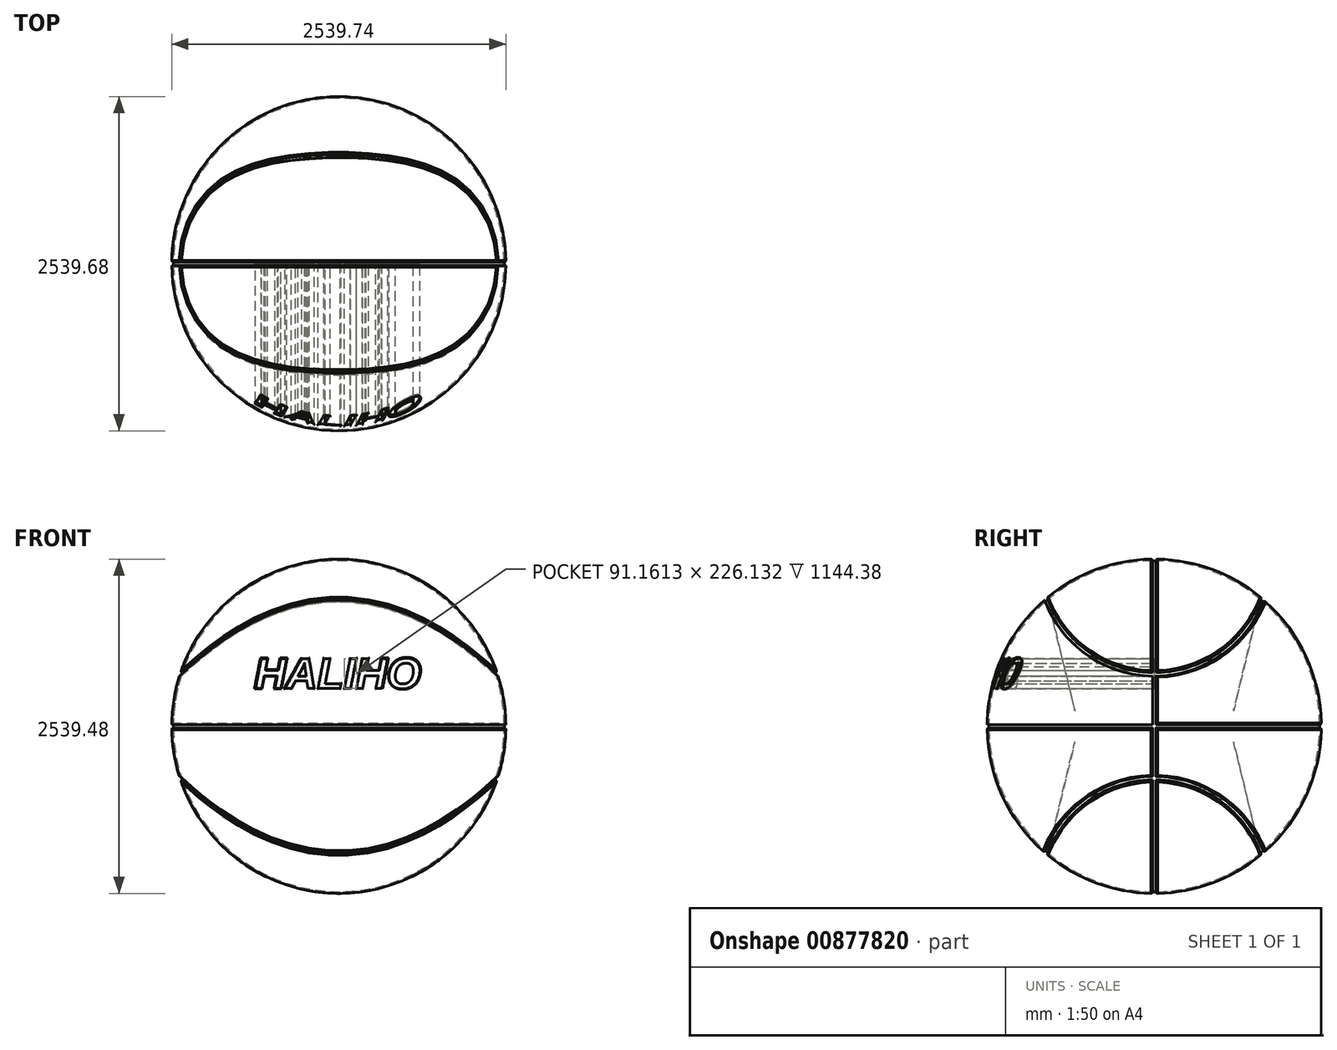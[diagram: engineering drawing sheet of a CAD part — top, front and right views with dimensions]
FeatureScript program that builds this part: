
annotation { "Feature Type Name" : "Feature", "Feature Type Description" : "" }
export const myFeature = defineFeature(function(context is Context, id is Id, definition is map)
    precondition{}
    {
        {
            var Q0;
            Q0=qCreatedBy(makeId("Front.planeOp"),FACE);
            var sketch = newSketch(context, id + "F0", { "sketchPlane" : qUnion([Q0])});
            skArc(sketch, "E0", {"start": v(1270, 0) * mm, "mid": v(0, 1270) * mm, "end": v(-1270, 0) * mm});
            skArc(sketch, "E1", {"start": v(1257.3, 0) * mm, "mid": v(0, 1257.3) * mm, "end": v(-1257.3, 0) * mm});
            skLineSegment(sketch, "E2", {"start": v(1270, 0) * mm, "end": v(-1270, 0) * mm});
            skLineSegment(sketch, "E3", {"start": v(0, 1270) * mm, "end": v(0, 1611.69) * mm});
            skPoint(sketch, "E3.startSnap0", {"position": v(0, 1270) * mm});
            skSolve(sketch);
        }
        {
            var Q0;
            {var subQ0=sQuery(id+"F0.wireOp",EDGE,"E0");Q0=makeQuery(id+"F0.imprint","IMPRINT",FACE,{"disambiguationData":[TD([[makeQuery(id+"F0.imprint","IMPRINT",EDGE,{"derivedFrom":subQ0}),1.0]])]});}
            var Q1;
            Q1=sQuery(id+"F0.wireOp",EDGE,"E2");
            revolve(context, id + "F1", {"surfaceOperationType" : NewSurfaceOperationType.NEW, "entities" : qUnion([Q0]), "axis" : qUnion([Q1]), "revolveType" : RevolveType.FULL});
        }
        {
            var Q0;
            Q0=qCreatedBy(makeId("Right.planeOp"),FACE);
            var sketch = newSketch(context, id + "F2", { "sketchPlane" : qUnion([Q0])});
            skLineSegment(sketch, "E4.bottom", {"start": v(1397, 12.7) * mm, "end": v(-1397, 12.7) * mm});
            skLineSegment(sketch, "E4.top", {"start": v(1397, -12.7) * mm, "end": v(-1397, -12.7) * mm});
            skLineSegment(sketch, "E4.left", {"start": v(1397, 12.7) * mm, "end": v(1397, -12.7) * mm});
            skLineSegment(sketch, "E4.right", {"start": v(-1397, 12.7) * mm, "end": v(-1397, -12.7) * mm});
            skPoint(sketch, "E4.middle", {"position": v(0, 0) * mm});
            skLineSegment(sketch, "E5.bottom", {"start": v(12.7, 1397) * mm, "end": v(-12.7, 1397) * mm});
            skLineSegment(sketch, "E5.top", {"start": v(12.7, -1397) * mm, "end": v(-12.7, -1397) * mm});
            skLineSegment(sketch, "E5.left", {"start": v(12.7, 1397) * mm, "end": v(12.7, -1397) * mm});
            skLineSegment(sketch, "E5.right", {"start": v(-12.7, 1397) * mm, "end": v(-12.7, -1397) * mm});
            skArc(sketch, "E6", {"start": v(-1269.94, 12.7) * mm, "mid": v(-1270, 0) * mm, "end": v(-1269.94, -12.7) * mm});
            skArc(sketch, "E7.trimOffspring", {"start": v(12.7, 1269.94) * mm, "mid": v(0, 1270) * mm, "end": v(-12.7, 1269.94) * mm});
            skArc(sketch, "E8.trimOffspring", {"start": v(1269.94, -12.7) * mm, "mid": v(1270, 0) * mm, "end": v(1269.94, 12.7) * mm});
            skArc(sketch, "E9.trimOffspring", {"start": v(-12.7, -1269.94) * mm, "mid": v(0, -1270) * mm, "end": v(12.7, -1269.94) * mm});
            skCircle(sketch, "E10", {"center": v(0, 1270) * mm, "radius": 889 * mm});
            skCircle(sketch, "E11", {"center": v(0, 1270) * mm, "radius": 863.6 * mm});
            skLineSegment(sketch, "E12", {"start": v(-1397, 0) * mm, "end": v(1397, 0) * mm, "construction": true});
            skCircle(sketch, "E13.MirrorC", {"center": v(0, -1270) * mm, "radius": 889 * mm});
            skCircle(sketch, "E14.MirrorC", {"center": v(0, -1270) * mm, "radius": 863.6 * mm});
            skSolve(sketch);
        }
        {
            var Q0;
            {var subQ0=sQuery(id+"F2.wireOp",EDGE,"E13.MirrorC");var subQ1=sQuery(id+"F2.wireOp",EDGE,"E5.left");var subQ2=makeQuery(id+"F2.imprint","INTERSECT",VERTEX,{"derivedFrom":[subQ1,subQ0]});Q0=makeQuery(id+"F2.imprint","IMPRINT",FACE,{"disambiguationData":[TD([[makeQuery(id+"F2.imprint","IMPRINT",EDGE,{"disambiguationData":[TD([[subQ2,-1.0]])],"derivedFrom":subQ1}),1.0]])]});}
            var Q1;
            {var subQ0=sQuery(id+"F2.wireOp",EDGE,"E10");var subQ1=sQuery(id+"F2.wireOp",EDGE,"E5.left");var subQ2=makeQuery(id+"F2.imprint","INTERSECT",VERTEX,{"derivedFrom":[subQ1,subQ0]});Q1=makeQuery(id+"F2.imprint","IMPRINT",FACE,{"disambiguationData":[TD([[makeQuery(id+"F2.imprint","IMPRINT",EDGE,{"disambiguationData":[TD([[subQ2,1.0]])],"derivedFrom":subQ1}),1.0]])]});}
            var Q2;
            {var subQ0=sQuery(id+"F2.wireOp",EDGE,"E13.MirrorC");var subQ1=sQuery(id+"F2.wireOp",EDGE,"E5.left");var subQ2=makeQuery(id+"F2.imprint","INTERSECT",VERTEX,{"derivedFrom":[subQ1,subQ0]});Q2=makeQuery(id+"F2.imprint","IMPRINT",FACE,{"disambiguationData":[TD([[makeQuery(id+"F2.imprint","IMPRINT",EDGE,{"disambiguationData":[TD([[subQ2,-1.0]])],"derivedFrom":subQ1}),-1.0]])]});}
            var Q3;
            {var subQ0=sQuery(id+"F2.wireOp",EDGE,"E10");var subQ1=sQuery(id+"F2.wireOp",EDGE,"E5.left");var subQ2=makeQuery(id+"F2.imprint","INTERSECT",VERTEX,{"derivedFrom":[subQ1,subQ0]});Q3=makeQuery(id+"F2.imprint","IMPRINT",FACE,{"disambiguationData":[TD([[makeQuery(id+"F2.imprint","IMPRINT",EDGE,{"disambiguationData":[TD([[subQ2,1.0]])],"derivedFrom":subQ1}),-1.0]])]});}
            var Q4;
            {var subQ0=sQuery(id+"F2.wireOp",EDGE,"E9.trimOffspring");Q4=makeQuery(id+"F2.imprint","IMPRINT",FACE,{"disambiguationData":[TD([[makeQuery(id+"F2.imprint","IMPRINT",EDGE,{"derivedFrom":subQ0}),1.0]])]});}
            var Q5;
            {var subQ0=sQuery(id+"F2.wireOp",EDGE,"E8.trimOffspring");Q5=makeQuery(id+"F2.imprint","IMPRINT",FACE,{"disambiguationData":[TD([[makeQuery(id+"F2.imprint","IMPRINT",EDGE,{"derivedFrom":subQ0}),1.0]])]});}
            var Q6;
            {var subQ0=sQuery(id+"F2.wireOp",EDGE,"E5.left");var subQ1=sQuery(id+"F2.wireOp",EDGE,"E4.top");var subQ2=makeQuery(id+"F2.imprint","INTERSECT",VERTEX,{"derivedFrom":[subQ1,subQ0]});Q6=makeQuery(id+"F2.imprint","IMPRINT",FACE,{"disambiguationData":[TD([[makeQuery(id+"F2.imprint","IMPRINT",EDGE,{"disambiguationData":[TD([[subQ2,-1.0]])],"derivedFrom":subQ1}),1.0]])]});}
            var Q7;
            {var subQ0=sQuery(id+"F2.wireOp",EDGE,"E6");Q7=makeQuery(id+"F2.imprint","IMPRINT",FACE,{"disambiguationData":[TD([[makeQuery(id+"F2.imprint","IMPRINT",EDGE,{"derivedFrom":subQ0}),1.0]])]});}
            var Q8;
            {var subQ0=sQuery(id+"F2.wireOp",EDGE,"E7.trimOffspring");Q8=makeQuery(id+"F2.imprint","IMPRINT",FACE,{"disambiguationData":[TD([[makeQuery(id+"F2.imprint","IMPRINT",EDGE,{"derivedFrom":subQ0}),1.0]])]});}
            var Q9;
            {var subQ0=sQuery(id+"F2.wireOp",EDGE,"E5.left");var subQ1=sQuery(id+"F2.wireOp",EDGE,"E4.bottom");var subQ2=makeQuery(id+"F2.imprint","INTERSECT",VERTEX,{"derivedFrom":[subQ1,subQ0]});Q9=makeQuery(id+"F2.imprint","IMPRINT",FACE,{"disambiguationData":[TD([[makeQuery(id+"F2.imprint","IMPRINT",EDGE,{"disambiguationData":[TD([[subQ2,-1.0]])],"derivedFrom":subQ1}),-1.0]])]});}
            var Q10;
            {var subQ0=sQuery(id+"F2.wireOp",EDGE,"E4.right");Q10=makeQuery(id+"F2.imprint","IMPRINT",FACE,{"disambiguationData":[TD([[makeQuery(id+"F2.imprint","IMPRINT",EDGE,{"derivedFrom":subQ0}),1.0]])]});}
            var Q11;
            {var subQ0=sQuery(id+"F2.wireOp",EDGE,"E4.left");Q11=makeQuery(id+"F2.imprint","IMPRINT",FACE,{"disambiguationData":[TD([[makeQuery(id+"F2.imprint","IMPRINT",EDGE,{"derivedFrom":subQ0}),-1.0]])]});}
            var Q12;
            {var subQ0=sQuery(id+"F2.wireOp",EDGE,"E5.bottom");Q12=makeQuery(id+"F2.imprint","IMPRINT",FACE,{"disambiguationData":[TD([[makeQuery(id+"F2.imprint","IMPRINT",EDGE,{"derivedFrom":subQ0}),1.0]])]});}
            var Q13;
            {var subQ0=sQuery(id+"F2.wireOp",EDGE,"E5.top");Q13=makeQuery(id+"F2.imprint","IMPRINT",FACE,{"disambiguationData":[TD([[makeQuery(id+"F2.imprint","IMPRINT",EDGE,{"derivedFrom":subQ0}),-1.0]])]});}
            var Q14;
            {var subQ0=sQuery(id+"F2.wireOp",EDGE,"E5.left");var subQ1=sQuery(id+"F2.wireOp",EDGE,"E4.bottom");var subQ2=makeQuery(id+"F2.imprint","INTERSECT",VERTEX,{"derivedFrom":[subQ1,subQ0]});Q14=makeQuery(id+"F2.imprint","IMPRINT",FACE,{"disambiguationData":[TD([[makeQuery(id+"F2.imprint","IMPRINT",EDGE,{"disambiguationData":[TD([[subQ2,-1.0]])],"derivedFrom":subQ1}),1.0]])]});}
            extrude(context, id + "F3", {"entities" : qUnion([Q0, Q1, Q2, Q3, Q4, Q5, Q6, Q7, Q8, Q9, Q10, Q11, Q12, Q13, Q14]), "operationType" : NewBodyOperationType.REMOVE, "oppositeDirection" : true, "depth" : 5638.8 * mm, "offsetDistance" : 25.4 * mm, "symmetric" : true});
        }
        {
            var Q0;
            {var subQ0=sQuery(id+"F0.wireOp",EDGE,"E1");Q0=makeQuery(id+"F0.imprint","IMPRINT",FACE,{"disambiguationData":[TD([[makeQuery(id+"F0.imprint","IMPRINT",EDGE,{"derivedFrom":subQ0}),1.0]])]});}
            var Q1;
            Q1=sQuery(id+"F0.wireOp",EDGE,"E2");
            revolve(context, id + "F4", {"surfaceOperationType" : NewSurfaceOperationType.NEW, "entities" : qUnion([Q0]), "axis" : qUnion([Q1]), "revolveType" : RevolveType.FULL});
        }
        {
            var Q0;
            Q0=qCreatedBy(makeId("Front.planeOp"),FACE);
            var sketch = newSketch(context, id + "F5", { "sketchPlane" : qUnion([Q0])});
            skText(sketch, "E15", { "text": "HALIHO", "fontName": "Arimo-BoldItalic.ttf"});
            const initialGuessF5  = {"E15": [-0.63861, 0.2874, 1, 0, 0.23666]};
            skSetInitialGuess(sketch, initialGuessF5);
            skSolve(sketch);
        }
        {
            var Q0;
            Q0 = qSketchRegion(id + "F5", true);
            extrude(context, id + "F6", {"entities" : qUnion([Q0]), "operationType" : NewBodyOperationType.REMOVE, "depth" : 3002.28 * mm, "offsetDistance" : 25.4 * mm});
        }
        {
            var Q0;
            {var subQ0=sQuery(id+"F2.wireOp",EDGE,"E5.right");var subQ1=makeQuery(id+"F2.imprint","INTERSECT",VERTEX,{"derivedFrom":[subQ0,sQuery(id+"F2.wireOp",EDGE,"E7.trimOffspring")]});Q0=makeQuery(id+"F3.boolean.opBoolean","SPLIT",FACE,{"disambiguationData":[TD([makeQuery(id+"F3.opExtrude","SWEPT_FACE",FACE,{"disambiguationData":[OSD([subQ0]),TDD([makeQuery(id+"F2.imprint","IMPRINT",EDGE,{"disambiguationData":[TD([[makeQuery(id+"F2.imprint","INTERSECT",VERTEX,{"derivedFrom":[sQuery(id+"F2.wireOp",EDGE,"E5.bottom"),subQ0]}),-1.0]])],"derivedFrom":subQ0}),makeQuery(id+"F2.imprint","IMPRINT",EDGE,{"disambiguationData":[TD([[subQ1,-1.0]])],"derivedFrom":subQ0})])]})])],"derivedFrom":makeQuery(id+"F1.opRevolve","SWEPT_FACE",FACE,{"disambiguationData":[OSD([sQuery(id+"F0.wireOp",EDGE,"E0")])]})});}
            var Q1;
            {var subQ0=sQuery(id+"F2.wireOp",EDGE,"E5.left");var subQ1=makeQuery(id+"F2.imprint","INTERSECT",VERTEX,{"derivedFrom":[subQ0,sQuery(id+"F2.wireOp",EDGE,"E7.trimOffspring")]});Q1=makeQuery(id+"F3.boolean.opBoolean","SPLIT",FACE,{"disambiguationData":[TD([makeQuery(id+"F3.opExtrude","SWEPT_FACE",FACE,{"disambiguationData":[OSD([subQ0]),TDD([makeQuery(id+"F2.imprint","IMPRINT",EDGE,{"disambiguationData":[TD([[makeQuery(id+"F2.imprint","INTERSECT",VERTEX,{"derivedFrom":[sQuery(id+"F2.wireOp",EDGE,"E5.bottom"),subQ0]}),-1.0]])],"derivedFrom":subQ0}),makeQuery(id+"F2.imprint","IMPRINT",EDGE,{"disambiguationData":[TD([[subQ1,-1.0]])],"derivedFrom":subQ0})])]})])],"derivedFrom":makeQuery(id+"F1.opRevolve","SWEPT_FACE",FACE,{"disambiguationData":[OSD([sQuery(id+"F0.wireOp",EDGE,"E0")])]})});}
            var Q2;
            {var subQ0=sQuery(id+"F2.wireOp",EDGE,"E4.bottom");var subQ2=sQuery(id+"F2.wireOp",EDGE,"E5.left");var subQ3=makeQuery(id+"F2.imprint","INTERSECT",VERTEX,{"derivedFrom":[subQ0,subQ2]});Q2=makeQuery(id+"F3.boolean.opBoolean","SPLIT",FACE,{"disambiguationData":[TD([makeQuery(id+"F3.opExtrude","SWEPT_FACE",FACE,{"disambiguationData":[OSD([subQ2]),TDD([makeQuery(id+"F2.imprint","IMPRINT",EDGE,{"disambiguationData":[TD([[subQ3,1.0]])],"derivedFrom":subQ2})])]})])],"derivedFrom":makeQuery(id+"F1.opRevolve","SWEPT_FACE",FACE,{"disambiguationData":[OSD([sQuery(id+"F0.wireOp",EDGE,"E0")])]})});}
            var Q3;
            {var subQ0=sQuery(id+"F2.wireOp",EDGE,"E4.top");var subQ2=sQuery(id+"F2.wireOp",EDGE,"E5.left");var subQ3=makeQuery(id+"F2.imprint","INTERSECT",VERTEX,{"derivedFrom":[subQ0,subQ2]});Q3=makeQuery(id+"F3.boolean.opBoolean","SPLIT",FACE,{"disambiguationData":[TD([makeQuery(id+"F3.opExtrude","SWEPT_FACE",FACE,{"disambiguationData":[OSD([subQ2]),TDD([makeQuery(id+"F2.imprint","IMPRINT",EDGE,{"disambiguationData":[TD([[subQ3,-1.0]])],"derivedFrom":subQ2})])]})])],"derivedFrom":makeQuery(id+"F1.opRevolve","SWEPT_FACE",FACE,{"disambiguationData":[OSD([sQuery(id+"F0.wireOp",EDGE,"E0")])]})});}
            var Q4;
            {var subQ0=sQuery(id+"F2.wireOp",EDGE,"E5.left");var subQ1=makeQuery(id+"F2.imprint","INTERSECT",VERTEX,{"derivedFrom":[subQ0,sQuery(id+"F2.wireOp",EDGE,"E9.trimOffspring")]});Q4=makeQuery(id+"F3.boolean.opBoolean","SPLIT",FACE,{"disambiguationData":[TD([makeQuery(id+"F3.opExtrude","SWEPT_FACE",FACE,{"disambiguationData":[OSD([subQ0]),TDD([makeQuery(id+"F2.imprint","IMPRINT",EDGE,{"disambiguationData":[TD([[subQ1,1.0]])],"derivedFrom":subQ0}),makeQuery(id+"F2.imprint","IMPRINT",EDGE,{"disambiguationData":[TD([[makeQuery(id+"F2.imprint","INTERSECT",VERTEX,{"derivedFrom":[sQuery(id+"F2.wireOp",EDGE,"E5.top"),subQ0]}),1.0]])],"derivedFrom":subQ0})])]})])],"derivedFrom":makeQuery(id+"F1.opRevolve","SWEPT_FACE",FACE,{"disambiguationData":[OSD([sQuery(id+"F0.wireOp",EDGE,"E0")])]})});}
            var Q5;
            {var subQ0=sQuery(id+"F2.wireOp",EDGE,"E5.right");var subQ1=makeQuery(id+"F2.imprint","INTERSECT",VERTEX,{"derivedFrom":[subQ0,sQuery(id+"F2.wireOp",EDGE,"E9.trimOffspring")]});Q5=makeQuery(id+"F3.boolean.opBoolean","SPLIT",FACE,{"disambiguationData":[TD([makeQuery(id+"F3.opExtrude","SWEPT_FACE",FACE,{"disambiguationData":[OSD([subQ0]),TDD([makeQuery(id+"F2.imprint","IMPRINT",EDGE,{"disambiguationData":[TD([[subQ1,1.0]])],"derivedFrom":subQ0}),makeQuery(id+"F2.imprint","IMPRINT",EDGE,{"disambiguationData":[TD([[makeQuery(id+"F2.imprint","INTERSECT",VERTEX,{"derivedFrom":[sQuery(id+"F2.wireOp",EDGE,"E5.top"),subQ0]}),1.0]])],"derivedFrom":subQ0})])]})])],"derivedFrom":makeQuery(id+"F1.opRevolve","SWEPT_FACE",FACE,{"disambiguationData":[OSD([sQuery(id+"F0.wireOp",EDGE,"E0")])]})});}
            var Q6;
            {var subQ0=sQuery(id+"F2.wireOp",EDGE,"E4.top");var subQ2=sQuery(id+"F2.wireOp",EDGE,"E5.right");var subQ3=makeQuery(id+"F2.imprint","INTERSECT",VERTEX,{"derivedFrom":[subQ0,subQ2]});Q6=makeQuery(id+"F3.boolean.opBoolean","SPLIT",FACE,{"disambiguationData":[TD([makeQuery(id+"F3.opExtrude","SWEPT_FACE",FACE,{"disambiguationData":[OSD([subQ2]),TDD([makeQuery(id+"F2.imprint","IMPRINT",EDGE,{"disambiguationData":[TD([[subQ3,-1.0]])],"derivedFrom":subQ2})])]})])],"derivedFrom":makeQuery(id+"F1.opRevolve","SWEPT_FACE",FACE,{"disambiguationData":[OSD([sQuery(id+"F0.wireOp",EDGE,"E0")])]})});}
            var Q7;
            {var subQ0=sQuery(id+"F2.wireOp",EDGE,"E4.bottom");var subQ2=sQuery(id+"F2.wireOp",EDGE,"E5.right");var subQ3=makeQuery(id+"F2.imprint","INTERSECT",VERTEX,{"derivedFrom":[subQ0,subQ2]});Q7=makeQuery(id+"F6.boolean.opBoolean","INTERSECT",EDGE,{"derivedFrom":[makeQuery(id+"F3.boolean.opBoolean","SPLIT",FACE,{"disambiguationData":[TD([makeQuery(id+"F3.opExtrude","SWEPT_FACE",FACE,{"disambiguationData":[OSD([subQ2]),TDD([makeQuery(id+"F2.imprint","IMPRINT",EDGE,{"disambiguationData":[TD([[subQ3,1.0]])],"derivedFrom":subQ2})])]})])],"derivedFrom":makeQuery(id+"F1.opRevolve","SWEPT_FACE",FACE,{"disambiguationData":[OSD([sQuery(id+"F0.wireOp",EDGE,"E1")])]})}),makeQuery(id+"F6.opExtrude","SWEPT_FACE",FACE,{"disambiguationData":[OSD([sQuery(id+"F5.wireOp",EDGE,"E15.sketch_text.stroke-48")])]})]});}
            var Q8;
            {var subQ0=sQuery(id+"F2.wireOp",EDGE,"E4.bottom");var subQ1=makeQuery(id+"F2.imprint","INTERSECT",VERTEX,{"derivedFrom":[subQ0,sQuery(id+"F2.wireOp",EDGE,"E6")]});Q8=makeQuery(id+"F3.boolean.opBoolean","INTERSECT",EDGE,{"derivedFrom":[makeQuery(id+"F1.opRevolve","SWEPT_FACE",FACE,{"disambiguationData":[OSD([sQuery(id+"F0.wireOp",EDGE,"E0")])]}),makeQuery(id+"F3.opExtrude","SWEPT_FACE",FACE,{"disambiguationData":[OSD([subQ0]),TDD([makeQuery(id+"F2.imprint","IMPRINT",EDGE,{"disambiguationData":[TD([[subQ1,1.0]])],"derivedFrom":subQ0}),makeQuery(id+"F2.imprint","IMPRINT",EDGE,{"disambiguationData":[TD([[makeQuery(id+"F2.imprint","INTERSECT",VERTEX,{"derivedFrom":[subQ0,sQuery(id+"F2.wireOp",EDGE,"E4.right")]}),1.0]])],"derivedFrom":subQ0})])]})]});}
            fillet(context, id + "F7", {"entities" : qUnion([Q0, Q1, Q2, Q3, Q4, Q5, Q6, Q7, Q8]), "radius" : 12.7 * mm, "allowEdgeOverflow" : false});
        }
        {
            var Q0;
            {var subQ0=sQuery(id+"F2.wireOp",EDGE,"E4.bottom");var subQ2=sQuery(id+"F2.wireOp",EDGE,"E5.right");var subQ3=makeQuery(id+"F2.imprint","INTERSECT",VERTEX,{"derivedFrom":[subQ0,subQ2]});Q0=makeQuery(id+"F6.boolean.opBoolean","INTERSECT",EDGE,{"derivedFrom":[makeQuery(id+"F3.boolean.opBoolean","SPLIT",FACE,{"disambiguationData":[TD([makeQuery(id+"F3.opExtrude","SWEPT_FACE",FACE,{"disambiguationData":[OSD([subQ2]),TDD([makeQuery(id+"F2.imprint","IMPRINT",EDGE,{"disambiguationData":[TD([[subQ3,1.0]])],"derivedFrom":subQ2})])]})])],"derivedFrom":makeQuery(id+"F1.opRevolve","SWEPT_FACE",FACE,{"disambiguationData":[OSD([sQuery(id+"F0.wireOp",EDGE,"E0")])]})}),makeQuery(id+"F6.opExtrude","SWEPT_FACE",FACE,{"disambiguationData":[OSD([sQuery(id+"F5.wireOp",EDGE,"E15.sketch_text.stroke-56")])]})]});}
            var Q1;
            {var subQ0=sQuery(id+"F2.wireOp",EDGE,"E4.bottom");var subQ2=sQuery(id+"F2.wireOp",EDGE,"E5.right");var subQ3=makeQuery(id+"F2.imprint","INTERSECT",VERTEX,{"derivedFrom":[subQ0,subQ2]});Q1=makeQuery(id+"F6.boolean.opBoolean","INTERSECT",EDGE,{"derivedFrom":[makeQuery(id+"F3.boolean.opBoolean","SPLIT",FACE,{"disambiguationData":[TD([makeQuery(id+"F3.opExtrude","SWEPT_FACE",FACE,{"disambiguationData":[OSD([subQ2]),TDD([makeQuery(id+"F2.imprint","IMPRINT",EDGE,{"disambiguationData":[TD([[subQ3,1.0]])],"derivedFrom":subQ2})])]})])],"derivedFrom":makeQuery(id+"F1.opRevolve","SWEPT_FACE",FACE,{"disambiguationData":[OSD([sQuery(id+"F0.wireOp",EDGE,"E0")])]})}),makeQuery(id+"F6.opExtrude","SWEPT_FACE",FACE,{"disambiguationData":[OSD([sQuery(id+"F5.wireOp",EDGE,"E15.sketch_text.stroke-55")])]})]});}
            var Q2;
            {var subQ0=sQuery(id+"F2.wireOp",EDGE,"E4.bottom");var subQ2=sQuery(id+"F2.wireOp",EDGE,"E5.right");var subQ3=makeQuery(id+"F2.imprint","INTERSECT",VERTEX,{"derivedFrom":[subQ0,subQ2]});Q2=makeQuery(id+"F6.boolean.opBoolean","INTERSECT",EDGE,{"derivedFrom":[makeQuery(id+"F3.boolean.opBoolean","SPLIT",FACE,{"disambiguationData":[TD([makeQuery(id+"F3.opExtrude","SWEPT_FACE",FACE,{"disambiguationData":[OSD([subQ2]),TDD([makeQuery(id+"F2.imprint","IMPRINT",EDGE,{"disambiguationData":[TD([[subQ3,1.0]])],"derivedFrom":subQ2})])]})])],"derivedFrom":makeQuery(id+"F1.opRevolve","SWEPT_FACE",FACE,{"disambiguationData":[OSD([sQuery(id+"F0.wireOp",EDGE,"E0")])]})}),makeQuery(id+"F6.opExtrude","SWEPT_FACE",FACE,{"disambiguationData":[OSD([sQuery(id+"F5.wireOp",EDGE,"E15.sketch_text.stroke-54")])]})]});}
            var Q3;
            {var subQ0=sQuery(id+"F2.wireOp",EDGE,"E4.bottom");var subQ2=sQuery(id+"F2.wireOp",EDGE,"E5.right");var subQ3=makeQuery(id+"F2.imprint","INTERSECT",VERTEX,{"derivedFrom":[subQ0,subQ2]});Q3=makeQuery(id+"F6.boolean.opBoolean","INTERSECT",EDGE,{"derivedFrom":[makeQuery(id+"F3.boolean.opBoolean","SPLIT",FACE,{"disambiguationData":[TD([makeQuery(id+"F3.opExtrude","SWEPT_FACE",FACE,{"disambiguationData":[OSD([subQ2]),TDD([makeQuery(id+"F2.imprint","IMPRINT",EDGE,{"disambiguationData":[TD([[subQ3,1.0]])],"derivedFrom":subQ2})])]})])],"derivedFrom":makeQuery(id+"F1.opRevolve","SWEPT_FACE",FACE,{"disambiguationData":[OSD([sQuery(id+"F0.wireOp",EDGE,"E0")])]})}),makeQuery(id+"F6.opExtrude","SWEPT_FACE",FACE,{"disambiguationData":[OSD([sQuery(id+"F5.wireOp",EDGE,"E15.sketch_text.stroke-53")])]})]});}
            var Q4;
            {var subQ0=sQuery(id+"F2.wireOp",EDGE,"E4.bottom");var subQ2=sQuery(id+"F2.wireOp",EDGE,"E5.right");var subQ3=makeQuery(id+"F2.imprint","INTERSECT",VERTEX,{"derivedFrom":[subQ0,subQ2]});Q4=makeQuery(id+"F6.boolean.opBoolean","INTERSECT",EDGE,{"derivedFrom":[makeQuery(id+"F3.boolean.opBoolean","SPLIT",FACE,{"disambiguationData":[TD([makeQuery(id+"F3.opExtrude","SWEPT_FACE",FACE,{"disambiguationData":[OSD([subQ2]),TDD([makeQuery(id+"F2.imprint","IMPRINT",EDGE,{"disambiguationData":[TD([[subQ3,1.0]])],"derivedFrom":subQ2})])]})])],"derivedFrom":makeQuery(id+"F1.opRevolve","SWEPT_FACE",FACE,{"disambiguationData":[OSD([sQuery(id+"F0.wireOp",EDGE,"E0")])]})}),makeQuery(id+"F6.opExtrude","SWEPT_FACE",FACE,{"disambiguationData":[OSD([sQuery(id+"F5.wireOp",EDGE,"E15.sketch_text.stroke-52")])]})]});}
            var Q5;
            {var subQ0=sQuery(id+"F2.wireOp",EDGE,"E4.bottom");var subQ2=sQuery(id+"F2.wireOp",EDGE,"E5.right");var subQ3=makeQuery(id+"F2.imprint","INTERSECT",VERTEX,{"derivedFrom":[subQ0,subQ2]});Q5=makeQuery(id+"F6.boolean.opBoolean","INTERSECT",EDGE,{"derivedFrom":[makeQuery(id+"F3.boolean.opBoolean","SPLIT",FACE,{"disambiguationData":[TD([makeQuery(id+"F3.opExtrude","SWEPT_FACE",FACE,{"disambiguationData":[OSD([subQ2]),TDD([makeQuery(id+"F2.imprint","IMPRINT",EDGE,{"disambiguationData":[TD([[subQ3,1.0]])],"derivedFrom":subQ2})])]})])],"derivedFrom":makeQuery(id+"F1.opRevolve","SWEPT_FACE",FACE,{"disambiguationData":[OSD([sQuery(id+"F0.wireOp",EDGE,"E0")])]})}),makeQuery(id+"F6.opExtrude","SWEPT_FACE",FACE,{"disambiguationData":[OSD([sQuery(id+"F5.wireOp",EDGE,"E15.sketch_text.stroke-45")])]})]});}
            var Q6;
            {var subQ0=sQuery(id+"F2.wireOp",EDGE,"E4.bottom");var subQ2=sQuery(id+"F2.wireOp",EDGE,"E5.right");var subQ3=makeQuery(id+"F2.imprint","INTERSECT",VERTEX,{"derivedFrom":[subQ0,subQ2]});Q6=makeQuery(id+"F6.boolean.opBoolean","INTERSECT",EDGE,{"derivedFrom":[makeQuery(id+"F3.boolean.opBoolean","SPLIT",FACE,{"disambiguationData":[TD([makeQuery(id+"F3.opExtrude","SWEPT_FACE",FACE,{"disambiguationData":[OSD([subQ2]),TDD([makeQuery(id+"F2.imprint","IMPRINT",EDGE,{"disambiguationData":[TD([[subQ3,1.0]])],"derivedFrom":subQ2})])]})])],"derivedFrom":makeQuery(id+"F1.opRevolve","SWEPT_FACE",FACE,{"disambiguationData":[OSD([sQuery(id+"F0.wireOp",EDGE,"E0")])]})}),makeQuery(id+"F6.opExtrude","SWEPT_FACE",FACE,{"disambiguationData":[OSD([sQuery(id+"F5.wireOp",EDGE,"E15.sketch_text.stroke-44")])]})]});}
            var Q7;
            {var subQ0=sQuery(id+"F2.wireOp",EDGE,"E4.bottom");var subQ2=sQuery(id+"F2.wireOp",EDGE,"E5.right");var subQ3=makeQuery(id+"F2.imprint","INTERSECT",VERTEX,{"derivedFrom":[subQ0,subQ2]});Q7=makeQuery(id+"F6.boolean.opBoolean","INTERSECT",EDGE,{"derivedFrom":[makeQuery(id+"F3.boolean.opBoolean","SPLIT",FACE,{"disambiguationData":[TD([makeQuery(id+"F3.opExtrude","SWEPT_FACE",FACE,{"disambiguationData":[OSD([subQ2]),TDD([makeQuery(id+"F2.imprint","IMPRINT",EDGE,{"disambiguationData":[TD([[subQ3,1.0]])],"derivedFrom":subQ2})])]})])],"derivedFrom":makeQuery(id+"F1.opRevolve","SWEPT_FACE",FACE,{"disambiguationData":[OSD([sQuery(id+"F0.wireOp",EDGE,"E0")])]})}),makeQuery(id+"F6.opExtrude","SWEPT_FACE",FACE,{"disambiguationData":[OSD([sQuery(id+"F5.wireOp",EDGE,"E15.sketch_text.stroke-43")])]})]});}
            var Q8;
            {var subQ0=sQuery(id+"F2.wireOp",EDGE,"E4.bottom");var subQ2=sQuery(id+"F2.wireOp",EDGE,"E5.right");var subQ3=makeQuery(id+"F2.imprint","INTERSECT",VERTEX,{"derivedFrom":[subQ0,subQ2]});Q8=makeQuery(id+"F6.boolean.opBoolean","INTERSECT",EDGE,{"derivedFrom":[makeQuery(id+"F3.boolean.opBoolean","SPLIT",FACE,{"disambiguationData":[TD([makeQuery(id+"F3.opExtrude","SWEPT_FACE",FACE,{"disambiguationData":[OSD([subQ2]),TDD([makeQuery(id+"F2.imprint","IMPRINT",EDGE,{"disambiguationData":[TD([[subQ3,1.0]])],"derivedFrom":subQ2})])]})])],"derivedFrom":makeQuery(id+"F1.opRevolve","SWEPT_FACE",FACE,{"disambiguationData":[OSD([sQuery(id+"F0.wireOp",EDGE,"E0")])]})}),makeQuery(id+"F6.opExtrude","SWEPT_FACE",FACE,{"disambiguationData":[OSD([sQuery(id+"F5.wireOp",EDGE,"E15.sketch_text.stroke-42")])]})]});}
            var Q9;
            {var subQ0=sQuery(id+"F2.wireOp",EDGE,"E4.bottom");var subQ2=sQuery(id+"F2.wireOp",EDGE,"E5.right");var subQ3=makeQuery(id+"F2.imprint","INTERSECT",VERTEX,{"derivedFrom":[subQ0,subQ2]});Q9=makeQuery(id+"F6.boolean.opBoolean","INTERSECT",EDGE,{"derivedFrom":[makeQuery(id+"F3.boolean.opBoolean","SPLIT",FACE,{"disambiguationData":[TD([makeQuery(id+"F3.opExtrude","SWEPT_FACE",FACE,{"disambiguationData":[OSD([subQ2]),TDD([makeQuery(id+"F2.imprint","IMPRINT",EDGE,{"disambiguationData":[TD([[subQ3,1.0]])],"derivedFrom":subQ2})])]})])],"derivedFrom":makeQuery(id+"F1.opRevolve","SWEPT_FACE",FACE,{"disambiguationData":[OSD([sQuery(id+"F0.wireOp",EDGE,"E0")])]})}),makeQuery(id+"F6.opExtrude","SWEPT_FACE",FACE,{"disambiguationData":[OSD([sQuery(id+"F5.wireOp",EDGE,"E15.sketch_text.stroke-41")])]})]});}
            var Q10;
            {var subQ0=sQuery(id+"F2.wireOp",EDGE,"E4.bottom");var subQ2=sQuery(id+"F2.wireOp",EDGE,"E5.right");var subQ3=makeQuery(id+"F2.imprint","INTERSECT",VERTEX,{"derivedFrom":[subQ0,subQ2]});Q10=makeQuery(id+"F6.boolean.opBoolean","INTERSECT",EDGE,{"derivedFrom":[makeQuery(id+"F3.boolean.opBoolean","SPLIT",FACE,{"disambiguationData":[TD([makeQuery(id+"F3.opExtrude","SWEPT_FACE",FACE,{"disambiguationData":[OSD([subQ2]),TDD([makeQuery(id+"F2.imprint","IMPRINT",EDGE,{"disambiguationData":[TD([[subQ3,1.0]])],"derivedFrom":subQ2})])]})])],"derivedFrom":makeQuery(id+"F1.opRevolve","SWEPT_FACE",FACE,{"disambiguationData":[OSD([sQuery(id+"F0.wireOp",EDGE,"E0")])]})}),makeQuery(id+"F6.opExtrude","SWEPT_FACE",FACE,{"disambiguationData":[OSD([sQuery(id+"F5.wireOp",EDGE,"E15.sketch_text.stroke-40")])]})]});}
            var Q11;
            {var subQ0=sQuery(id+"F2.wireOp",EDGE,"E4.bottom");var subQ2=sQuery(id+"F2.wireOp",EDGE,"E5.right");var subQ3=makeQuery(id+"F2.imprint","INTERSECT",VERTEX,{"derivedFrom":[subQ0,subQ2]});Q11=makeQuery(id+"F6.boolean.opBoolean","INTERSECT",EDGE,{"derivedFrom":[makeQuery(id+"F3.boolean.opBoolean","SPLIT",FACE,{"disambiguationData":[TD([makeQuery(id+"F3.opExtrude","SWEPT_FACE",FACE,{"disambiguationData":[OSD([subQ2]),TDD([makeQuery(id+"F2.imprint","IMPRINT",EDGE,{"disambiguationData":[TD([[subQ3,1.0]])],"derivedFrom":subQ2})])]})])],"derivedFrom":makeQuery(id+"F1.opRevolve","SWEPT_FACE",FACE,{"disambiguationData":[OSD([sQuery(id+"F0.wireOp",EDGE,"E0")])]})}),makeQuery(id+"F6.opExtrude","SWEPT_FACE",FACE,{"disambiguationData":[OSD([sQuery(id+"F5.wireOp",EDGE,"E15.sketch_text.stroke-39")])]})]});}
            var Q12;
            {var subQ0=sQuery(id+"F2.wireOp",EDGE,"E4.bottom");var subQ2=sQuery(id+"F2.wireOp",EDGE,"E5.right");var subQ3=makeQuery(id+"F2.imprint","INTERSECT",VERTEX,{"derivedFrom":[subQ0,subQ2]});Q12=makeQuery(id+"F6.boolean.opBoolean","INTERSECT",EDGE,{"derivedFrom":[makeQuery(id+"F3.boolean.opBoolean","SPLIT",FACE,{"disambiguationData":[TD([makeQuery(id+"F3.opExtrude","SWEPT_FACE",FACE,{"disambiguationData":[OSD([subQ2]),TDD([makeQuery(id+"F2.imprint","IMPRINT",EDGE,{"disambiguationData":[TD([[subQ3,1.0]])],"derivedFrom":subQ2})])]})])],"derivedFrom":makeQuery(id+"F1.opRevolve","SWEPT_FACE",FACE,{"disambiguationData":[OSD([sQuery(id+"F0.wireOp",EDGE,"E0")])]})}),makeQuery(id+"F6.opExtrude","SWEPT_FACE",FACE,{"disambiguationData":[OSD([sQuery(id+"F5.wireOp",EDGE,"E15.sketch_text.stroke-38")])]})]});}
            var Q13;
            {var subQ0=sQuery(id+"F2.wireOp",EDGE,"E4.bottom");var subQ2=sQuery(id+"F2.wireOp",EDGE,"E5.right");var subQ3=makeQuery(id+"F2.imprint","INTERSECT",VERTEX,{"derivedFrom":[subQ0,subQ2]});Q13=makeQuery(id+"F6.boolean.opBoolean","INTERSECT",EDGE,{"derivedFrom":[makeQuery(id+"F3.boolean.opBoolean","SPLIT",FACE,{"disambiguationData":[TD([makeQuery(id+"F3.opExtrude","SWEPT_FACE",FACE,{"disambiguationData":[OSD([subQ2]),TDD([makeQuery(id+"F2.imprint","IMPRINT",EDGE,{"disambiguationData":[TD([[subQ3,1.0]])],"derivedFrom":subQ2})])]})])],"derivedFrom":makeQuery(id+"F1.opRevolve","SWEPT_FACE",FACE,{"disambiguationData":[OSD([sQuery(id+"F0.wireOp",EDGE,"E0")])]})}),makeQuery(id+"F6.opExtrude","SWEPT_FACE",FACE,{"disambiguationData":[OSD([sQuery(id+"F5.wireOp",EDGE,"E15.sketch_text.stroke-37")])]})]});}
            var Q14;
            {var subQ0=sQuery(id+"F2.wireOp",EDGE,"E4.bottom");var subQ2=sQuery(id+"F2.wireOp",EDGE,"E5.right");var subQ3=makeQuery(id+"F2.imprint","INTERSECT",VERTEX,{"derivedFrom":[subQ0,subQ2]});Q14=makeQuery(id+"F6.boolean.opBoolean","INTERSECT",EDGE,{"derivedFrom":[makeQuery(id+"F3.boolean.opBoolean","SPLIT",FACE,{"disambiguationData":[TD([makeQuery(id+"F3.opExtrude","SWEPT_FACE",FACE,{"disambiguationData":[OSD([subQ2]),TDD([makeQuery(id+"F2.imprint","IMPRINT",EDGE,{"disambiguationData":[TD([[subQ3,1.0]])],"derivedFrom":subQ2})])]})])],"derivedFrom":makeQuery(id+"F1.opRevolve","SWEPT_FACE",FACE,{"disambiguationData":[OSD([sQuery(id+"F0.wireOp",EDGE,"E0")])]})}),makeQuery(id+"F6.opExtrude","SWEPT_FACE",FACE,{"disambiguationData":[OSD([sQuery(id+"F5.wireOp",EDGE,"E15.sketch_text.stroke-36")])]})]});}
            var Q15;
            {var subQ0=sQuery(id+"F2.wireOp",EDGE,"E4.bottom");var subQ2=sQuery(id+"F2.wireOp",EDGE,"E5.right");var subQ3=makeQuery(id+"F2.imprint","INTERSECT",VERTEX,{"derivedFrom":[subQ0,subQ2]});Q15=makeQuery(id+"F6.boolean.opBoolean","INTERSECT",EDGE,{"derivedFrom":[makeQuery(id+"F3.boolean.opBoolean","SPLIT",FACE,{"disambiguationData":[TD([makeQuery(id+"F3.opExtrude","SWEPT_FACE",FACE,{"disambiguationData":[OSD([subQ2]),TDD([makeQuery(id+"F2.imprint","IMPRINT",EDGE,{"disambiguationData":[TD([[subQ3,1.0]])],"derivedFrom":subQ2})])]})])],"derivedFrom":makeQuery(id+"F1.opRevolve","SWEPT_FACE",FACE,{"disambiguationData":[OSD([sQuery(id+"F0.wireOp",EDGE,"E0")])]})}),makeQuery(id+"F6.opExtrude","SWEPT_FACE",FACE,{"disambiguationData":[OSD([sQuery(id+"F5.wireOp",EDGE,"E15.sketch_text.stroke-35")])]})]});}
            var Q16;
            {var subQ0=sQuery(id+"F2.wireOp",EDGE,"E4.bottom");var subQ2=sQuery(id+"F2.wireOp",EDGE,"E5.right");var subQ3=makeQuery(id+"F2.imprint","INTERSECT",VERTEX,{"derivedFrom":[subQ0,subQ2]});Q16=makeQuery(id+"F6.boolean.opBoolean","INTERSECT",EDGE,{"derivedFrom":[makeQuery(id+"F3.boolean.opBoolean","SPLIT",FACE,{"disambiguationData":[TD([makeQuery(id+"F3.opExtrude","SWEPT_FACE",FACE,{"disambiguationData":[OSD([subQ2]),TDD([makeQuery(id+"F2.imprint","IMPRINT",EDGE,{"disambiguationData":[TD([[subQ3,1.0]])],"derivedFrom":subQ2})])]})])],"derivedFrom":makeQuery(id+"F1.opRevolve","SWEPT_FACE",FACE,{"disambiguationData":[OSD([sQuery(id+"F0.wireOp",EDGE,"E0")])]})}),makeQuery(id+"F6.opExtrude","SWEPT_FACE",FACE,{"disambiguationData":[OSD([sQuery(id+"F5.wireOp",EDGE,"E15.sketch_text.stroke-46")])]})]});}
            var Q17;
            {var subQ0=sQuery(id+"F2.wireOp",EDGE,"E4.bottom");var subQ2=sQuery(id+"F2.wireOp",EDGE,"E5.right");var subQ3=makeQuery(id+"F2.imprint","INTERSECT",VERTEX,{"derivedFrom":[subQ0,subQ2]});Q17=makeQuery(id+"F6.boolean.opBoolean","INTERSECT",EDGE,{"derivedFrom":[makeQuery(id+"F3.boolean.opBoolean","SPLIT",FACE,{"disambiguationData":[TD([makeQuery(id+"F3.opExtrude","SWEPT_FACE",FACE,{"disambiguationData":[OSD([subQ2]),TDD([makeQuery(id+"F2.imprint","IMPRINT",EDGE,{"disambiguationData":[TD([[subQ3,1.0]])],"derivedFrom":subQ2})])]})])],"derivedFrom":makeQuery(id+"F1.opRevolve","SWEPT_FACE",FACE,{"disambiguationData":[OSD([sQuery(id+"F0.wireOp",EDGE,"E0")])]})}),makeQuery(id+"F6.opExtrude","SWEPT_FACE",FACE,{"disambiguationData":[OSD([sQuery(id+"F5.wireOp",EDGE,"E15.sketch_text.stroke-32")])]})]});}
            var Q18;
            {var subQ0=sQuery(id+"F2.wireOp",EDGE,"E4.bottom");var subQ2=sQuery(id+"F2.wireOp",EDGE,"E5.right");var subQ3=makeQuery(id+"F2.imprint","INTERSECT",VERTEX,{"derivedFrom":[subQ0,subQ2]});Q18=makeQuery(id+"F6.boolean.opBoolean","INTERSECT",EDGE,{"derivedFrom":[makeQuery(id+"F3.boolean.opBoolean","SPLIT",FACE,{"disambiguationData":[TD([makeQuery(id+"F3.opExtrude","SWEPT_FACE",FACE,{"disambiguationData":[OSD([subQ2]),TDD([makeQuery(id+"F2.imprint","IMPRINT",EDGE,{"disambiguationData":[TD([[subQ3,1.0]])],"derivedFrom":subQ2})])]})])],"derivedFrom":makeQuery(id+"F1.opRevolve","SWEPT_FACE",FACE,{"disambiguationData":[OSD([sQuery(id+"F0.wireOp",EDGE,"E0")])]})}),makeQuery(id+"F6.opExtrude","SWEPT_FACE",FACE,{"disambiguationData":[OSD([sQuery(id+"F5.wireOp",EDGE,"E15.sketch_text.stroke-31")])]})]});}
            var Q19;
            {var subQ0=sQuery(id+"F2.wireOp",EDGE,"E4.bottom");var subQ2=sQuery(id+"F2.wireOp",EDGE,"E5.right");var subQ3=makeQuery(id+"F2.imprint","INTERSECT",VERTEX,{"derivedFrom":[subQ0,subQ2]});Q19=makeQuery(id+"F6.boolean.opBoolean","INTERSECT",EDGE,{"derivedFrom":[makeQuery(id+"F3.boolean.opBoolean","SPLIT",FACE,{"disambiguationData":[TD([makeQuery(id+"F3.opExtrude","SWEPT_FACE",FACE,{"disambiguationData":[OSD([subQ2]),TDD([makeQuery(id+"F2.imprint","IMPRINT",EDGE,{"disambiguationData":[TD([[subQ3,1.0]])],"derivedFrom":subQ2})])]})])],"derivedFrom":makeQuery(id+"F1.opRevolve","SWEPT_FACE",FACE,{"disambiguationData":[OSD([sQuery(id+"F0.wireOp",EDGE,"E0")])]})}),makeQuery(id+"F6.opExtrude","SWEPT_FACE",FACE,{"disambiguationData":[OSD([sQuery(id+"F5.wireOp",EDGE,"E15.sketch_text.stroke-34")])]})]});}
            var Q20;
            {var subQ0=sQuery(id+"F2.wireOp",EDGE,"E4.bottom");var subQ2=sQuery(id+"F2.wireOp",EDGE,"E5.right");var subQ3=makeQuery(id+"F2.imprint","INTERSECT",VERTEX,{"derivedFrom":[subQ0,subQ2]});Q20=makeQuery(id+"F6.boolean.opBoolean","INTERSECT",EDGE,{"derivedFrom":[makeQuery(id+"F3.boolean.opBoolean","SPLIT",FACE,{"disambiguationData":[TD([makeQuery(id+"F3.opExtrude","SWEPT_FACE",FACE,{"disambiguationData":[OSD([subQ2]),TDD([makeQuery(id+"F2.imprint","IMPRINT",EDGE,{"disambiguationData":[TD([[subQ3,1.0]])],"derivedFrom":subQ2})])]})])],"derivedFrom":makeQuery(id+"F1.opRevolve","SWEPT_FACE",FACE,{"disambiguationData":[OSD([sQuery(id+"F0.wireOp",EDGE,"E0")])]})}),makeQuery(id+"F6.opExtrude","SWEPT_FACE",FACE,{"disambiguationData":[OSD([sQuery(id+"F5.wireOp",EDGE,"E15.sketch_text.stroke-33")])]})]});}
            var Q21;
            {var subQ0=sQuery(id+"F2.wireOp",EDGE,"E4.bottom");var subQ2=sQuery(id+"F2.wireOp",EDGE,"E5.right");var subQ3=makeQuery(id+"F2.imprint","INTERSECT",VERTEX,{"derivedFrom":[subQ0,subQ2]});Q21=makeQuery(id+"F6.boolean.opBoolean","INTERSECT",EDGE,{"derivedFrom":[makeQuery(id+"F3.boolean.opBoolean","SPLIT",FACE,{"disambiguationData":[TD([makeQuery(id+"F3.opExtrude","SWEPT_FACE",FACE,{"disambiguationData":[OSD([subQ2]),TDD([makeQuery(id+"F2.imprint","IMPRINT",EDGE,{"disambiguationData":[TD([[subQ3,1.0]])],"derivedFrom":subQ2})])]})])],"derivedFrom":makeQuery(id+"F1.opRevolve","SWEPT_FACE",FACE,{"disambiguationData":[OSD([sQuery(id+"F0.wireOp",EDGE,"E0")])]})}),makeQuery(id+"F6.opExtrude","SWEPT_FACE",FACE,{"disambiguationData":[OSD([sQuery(id+"F5.wireOp",EDGE,"E15.sketch_text.stroke-29")])]})]});}
            var Q22;
            {var subQ0=sQuery(id+"F2.wireOp",EDGE,"E4.bottom");var subQ2=sQuery(id+"F2.wireOp",EDGE,"E5.right");var subQ3=makeQuery(id+"F2.imprint","INTERSECT",VERTEX,{"derivedFrom":[subQ0,subQ2]});Q22=makeQuery(id+"F6.boolean.opBoolean","INTERSECT",EDGE,{"derivedFrom":[makeQuery(id+"F3.boolean.opBoolean","SPLIT",FACE,{"disambiguationData":[TD([makeQuery(id+"F3.opExtrude","SWEPT_FACE",FACE,{"disambiguationData":[OSD([subQ2]),TDD([makeQuery(id+"F2.imprint","IMPRINT",EDGE,{"disambiguationData":[TD([[subQ3,1.0]])],"derivedFrom":subQ2})])]})])],"derivedFrom":makeQuery(id+"F1.opRevolve","SWEPT_FACE",FACE,{"disambiguationData":[OSD([sQuery(id+"F0.wireOp",EDGE,"E0")])]})}),makeQuery(id+"F6.opExtrude","SWEPT_FACE",FACE,{"disambiguationData":[OSD([sQuery(id+"F5.wireOp",EDGE,"E15.sketch_text.stroke-28")])]})]});}
            var Q23;
            {var subQ0=sQuery(id+"F2.wireOp",EDGE,"E4.bottom");var subQ2=sQuery(id+"F2.wireOp",EDGE,"E5.right");var subQ3=makeQuery(id+"F2.imprint","INTERSECT",VERTEX,{"derivedFrom":[subQ0,subQ2]});Q23=makeQuery(id+"F6.boolean.opBoolean","INTERSECT",EDGE,{"derivedFrom":[makeQuery(id+"F3.boolean.opBoolean","SPLIT",FACE,{"disambiguationData":[TD([makeQuery(id+"F3.opExtrude","SWEPT_FACE",FACE,{"disambiguationData":[OSD([subQ2]),TDD([makeQuery(id+"F2.imprint","IMPRINT",EDGE,{"disambiguationData":[TD([[subQ3,1.0]])],"derivedFrom":subQ2})])]})])],"derivedFrom":makeQuery(id+"F1.opRevolve","SWEPT_FACE",FACE,{"disambiguationData":[OSD([sQuery(id+"F0.wireOp",EDGE,"E0")])]})}),makeQuery(id+"F6.opExtrude","SWEPT_FACE",FACE,{"disambiguationData":[OSD([sQuery(id+"F5.wireOp",EDGE,"E15.sketch_text.stroke-27")])]})]});}
            var Q24;
            {var subQ0=sQuery(id+"F2.wireOp",EDGE,"E4.bottom");var subQ2=sQuery(id+"F2.wireOp",EDGE,"E5.right");var subQ3=makeQuery(id+"F2.imprint","INTERSECT",VERTEX,{"derivedFrom":[subQ0,subQ2]});Q24=makeQuery(id+"F6.boolean.opBoolean","INTERSECT",EDGE,{"derivedFrom":[makeQuery(id+"F3.boolean.opBoolean","SPLIT",FACE,{"disambiguationData":[TD([makeQuery(id+"F3.opExtrude","SWEPT_FACE",FACE,{"disambiguationData":[OSD([subQ2]),TDD([makeQuery(id+"F2.imprint","IMPRINT",EDGE,{"disambiguationData":[TD([[subQ3,1.0]])],"derivedFrom":subQ2})])]})])],"derivedFrom":makeQuery(id+"F1.opRevolve","SWEPT_FACE",FACE,{"disambiguationData":[OSD([sQuery(id+"F0.wireOp",EDGE,"E0")])]})}),makeQuery(id+"F6.opExtrude","SWEPT_FACE",FACE,{"disambiguationData":[OSD([sQuery(id+"F5.wireOp",EDGE,"E15.sketch_text.stroke-26")])]})]});}
            var Q25;
            {var subQ0=sQuery(id+"F2.wireOp",EDGE,"E4.bottom");var subQ2=sQuery(id+"F2.wireOp",EDGE,"E5.right");var subQ3=makeQuery(id+"F2.imprint","INTERSECT",VERTEX,{"derivedFrom":[subQ0,subQ2]});Q25=makeQuery(id+"F6.boolean.opBoolean","INTERSECT",EDGE,{"derivedFrom":[makeQuery(id+"F3.boolean.opBoolean","SPLIT",FACE,{"disambiguationData":[TD([makeQuery(id+"F3.opExtrude","SWEPT_FACE",FACE,{"disambiguationData":[OSD([subQ2]),TDD([makeQuery(id+"F2.imprint","IMPRINT",EDGE,{"disambiguationData":[TD([[subQ3,1.0]])],"derivedFrom":subQ2})])]})])],"derivedFrom":makeQuery(id+"F1.opRevolve","SWEPT_FACE",FACE,{"disambiguationData":[OSD([sQuery(id+"F0.wireOp",EDGE,"E0")])]})}),makeQuery(id+"F6.opExtrude","SWEPT_FACE",FACE,{"disambiguationData":[OSD([sQuery(id+"F5.wireOp",EDGE,"E15.sketch_text.stroke-25")])]})]});}
            var Q26;
            {var subQ0=sQuery(id+"F2.wireOp",EDGE,"E4.bottom");var subQ2=sQuery(id+"F2.wireOp",EDGE,"E5.right");var subQ3=makeQuery(id+"F2.imprint","INTERSECT",VERTEX,{"derivedFrom":[subQ0,subQ2]});Q26=makeQuery(id+"F6.boolean.opBoolean","INTERSECT",EDGE,{"derivedFrom":[makeQuery(id+"F3.boolean.opBoolean","SPLIT",FACE,{"disambiguationData":[TD([makeQuery(id+"F3.opExtrude","SWEPT_FACE",FACE,{"disambiguationData":[OSD([subQ2]),TDD([makeQuery(id+"F2.imprint","IMPRINT",EDGE,{"disambiguationData":[TD([[subQ3,1.0]])],"derivedFrom":subQ2})])]})])],"derivedFrom":makeQuery(id+"F1.opRevolve","SWEPT_FACE",FACE,{"disambiguationData":[OSD([sQuery(id+"F0.wireOp",EDGE,"E0")])]})}),makeQuery(id+"F6.opExtrude","SWEPT_FACE",FACE,{"disambiguationData":[OSD([sQuery(id+"F5.wireOp",EDGE,"E15.sketch_text.stroke-30")])]})]});}
            var Q27;
            {var subQ0=sQuery(id+"F2.wireOp",EDGE,"E4.bottom");var subQ2=sQuery(id+"F2.wireOp",EDGE,"E5.right");var subQ3=makeQuery(id+"F2.imprint","INTERSECT",VERTEX,{"derivedFrom":[subQ0,subQ2]});Q27=makeQuery(id+"F6.boolean.opBoolean","INTERSECT",EDGE,{"derivedFrom":[makeQuery(id+"F3.boolean.opBoolean","SPLIT",FACE,{"disambiguationData":[TD([makeQuery(id+"F3.opExtrude","SWEPT_FACE",FACE,{"disambiguationData":[OSD([subQ2]),TDD([makeQuery(id+"F2.imprint","IMPRINT",EDGE,{"disambiguationData":[TD([[subQ3,1.0]])],"derivedFrom":subQ2})])]})])],"derivedFrom":makeQuery(id+"F1.opRevolve","SWEPT_FACE",FACE,{"disambiguationData":[OSD([sQuery(id+"F0.wireOp",EDGE,"E0")])]})}),makeQuery(id+"F6.opExtrude","SWEPT_FACE",FACE,{"disambiguationData":[OSD([sQuery(id+"F5.wireOp",EDGE,"E15.sketch_text.stroke-19")])]})]});}
            var Q28;
            {var subQ0=sQuery(id+"F2.wireOp",EDGE,"E4.bottom");var subQ2=sQuery(id+"F2.wireOp",EDGE,"E5.right");var subQ3=makeQuery(id+"F2.imprint","INTERSECT",VERTEX,{"derivedFrom":[subQ0,subQ2]});Q28=makeQuery(id+"F6.boolean.opBoolean","INTERSECT",EDGE,{"derivedFrom":[makeQuery(id+"F3.boolean.opBoolean","SPLIT",FACE,{"disambiguationData":[TD([makeQuery(id+"F3.opExtrude","SWEPT_FACE",FACE,{"disambiguationData":[OSD([subQ2]),TDD([makeQuery(id+"F2.imprint","IMPRINT",EDGE,{"disambiguationData":[TD([[subQ3,1.0]])],"derivedFrom":subQ2})])]})])],"derivedFrom":makeQuery(id+"F1.opRevolve","SWEPT_FACE",FACE,{"disambiguationData":[OSD([sQuery(id+"F0.wireOp",EDGE,"E0")])]})}),makeQuery(id+"F6.opExtrude","SWEPT_FACE",FACE,{"disambiguationData":[OSD([sQuery(id+"F5.wireOp",EDGE,"E15.sketch_text.stroke-18")])]})]});}
            var Q29;
            {var subQ0=sQuery(id+"F2.wireOp",EDGE,"E4.bottom");var subQ2=sQuery(id+"F2.wireOp",EDGE,"E5.right");var subQ3=makeQuery(id+"F2.imprint","INTERSECT",VERTEX,{"derivedFrom":[subQ0,subQ2]});Q29=makeQuery(id+"F6.boolean.opBoolean","INTERSECT",EDGE,{"derivedFrom":[makeQuery(id+"F3.boolean.opBoolean","SPLIT",FACE,{"disambiguationData":[TD([makeQuery(id+"F3.opExtrude","SWEPT_FACE",FACE,{"disambiguationData":[OSD([subQ2]),TDD([makeQuery(id+"F2.imprint","IMPRINT",EDGE,{"disambiguationData":[TD([[subQ3,1.0]])],"derivedFrom":subQ2})])]})])],"derivedFrom":makeQuery(id+"F1.opRevolve","SWEPT_FACE",FACE,{"disambiguationData":[OSD([sQuery(id+"F0.wireOp",EDGE,"E0")])]})}),makeQuery(id+"F6.opExtrude","SWEPT_FACE",FACE,{"disambiguationData":[OSD([sQuery(id+"F5.wireOp",EDGE,"E15.sketch_text.stroke-17")])]})]});}
            var Q30;
            {var subQ0=sQuery(id+"F2.wireOp",EDGE,"E4.bottom");var subQ2=sQuery(id+"F2.wireOp",EDGE,"E5.right");var subQ3=makeQuery(id+"F2.imprint","INTERSECT",VERTEX,{"derivedFrom":[subQ0,subQ2]});Q30=makeQuery(id+"F6.boolean.opBoolean","INTERSECT",EDGE,{"derivedFrom":[makeQuery(id+"F3.boolean.opBoolean","SPLIT",FACE,{"disambiguationData":[TD([makeQuery(id+"F3.opExtrude","SWEPT_FACE",FACE,{"disambiguationData":[OSD([subQ2]),TDD([makeQuery(id+"F2.imprint","IMPRINT",EDGE,{"disambiguationData":[TD([[subQ3,1.0]])],"derivedFrom":subQ2})])]})])],"derivedFrom":makeQuery(id+"F1.opRevolve","SWEPT_FACE",FACE,{"disambiguationData":[OSD([sQuery(id+"F0.wireOp",EDGE,"E0")])]})}),makeQuery(id+"F6.opExtrude","SWEPT_FACE",FACE,{"disambiguationData":[OSD([sQuery(id+"F5.wireOp",EDGE,"E15.sketch_text.stroke-16")])]})]});}
            var Q31;
            {var subQ0=sQuery(id+"F2.wireOp",EDGE,"E4.bottom");var subQ2=sQuery(id+"F2.wireOp",EDGE,"E5.right");var subQ3=makeQuery(id+"F2.imprint","INTERSECT",VERTEX,{"derivedFrom":[subQ0,subQ2]});Q31=makeQuery(id+"F6.boolean.opBoolean","INTERSECT",EDGE,{"derivedFrom":[makeQuery(id+"F3.boolean.opBoolean","SPLIT",FACE,{"disambiguationData":[TD([makeQuery(id+"F3.opExtrude","SWEPT_FACE",FACE,{"disambiguationData":[OSD([subQ2]),TDD([makeQuery(id+"F2.imprint","IMPRINT",EDGE,{"disambiguationData":[TD([[subQ3,1.0]])],"derivedFrom":subQ2})])]})])],"derivedFrom":makeQuery(id+"F1.opRevolve","SWEPT_FACE",FACE,{"disambiguationData":[OSD([sQuery(id+"F0.wireOp",EDGE,"E0")])]})}),makeQuery(id+"F6.opExtrude","SWEPT_FACE",FACE,{"disambiguationData":[OSD([sQuery(id+"F5.wireOp",EDGE,"E15.sketch_text.stroke-15")])]})]});}
            var Q32;
            {var subQ0=sQuery(id+"F2.wireOp",EDGE,"E4.bottom");var subQ2=sQuery(id+"F2.wireOp",EDGE,"E5.right");var subQ3=makeQuery(id+"F2.imprint","INTERSECT",VERTEX,{"derivedFrom":[subQ0,subQ2]});Q32=makeQuery(id+"F6.boolean.opBoolean","INTERSECT",EDGE,{"derivedFrom":[makeQuery(id+"F3.boolean.opBoolean","SPLIT",FACE,{"disambiguationData":[TD([makeQuery(id+"F3.opExtrude","SWEPT_FACE",FACE,{"disambiguationData":[OSD([subQ2]),TDD([makeQuery(id+"F2.imprint","IMPRINT",EDGE,{"disambiguationData":[TD([[subQ3,1.0]])],"derivedFrom":subQ2})])]})])],"derivedFrom":makeQuery(id+"F1.opRevolve","SWEPT_FACE",FACE,{"disambiguationData":[OSD([sQuery(id+"F0.wireOp",EDGE,"E0")])]})}),makeQuery(id+"F6.opExtrude","SWEPT_FACE",FACE,{"disambiguationData":[OSD([sQuery(id+"F5.wireOp",EDGE,"E15.sketch_text.stroke-14")])]})]});}
            var Q33;
            {var subQ0=sQuery(id+"F2.wireOp",EDGE,"E4.bottom");var subQ2=sQuery(id+"F2.wireOp",EDGE,"E5.right");var subQ3=makeQuery(id+"F2.imprint","INTERSECT",VERTEX,{"derivedFrom":[subQ0,subQ2]});Q33=makeQuery(id+"F6.boolean.opBoolean","INTERSECT",EDGE,{"derivedFrom":[makeQuery(id+"F3.boolean.opBoolean","SPLIT",FACE,{"disambiguationData":[TD([makeQuery(id+"F3.opExtrude","SWEPT_FACE",FACE,{"disambiguationData":[OSD([subQ2]),TDD([makeQuery(id+"F2.imprint","IMPRINT",EDGE,{"disambiguationData":[TD([[subQ3,1.0]])],"derivedFrom":subQ2})])]})])],"derivedFrom":makeQuery(id+"F1.opRevolve","SWEPT_FACE",FACE,{"disambiguationData":[OSD([sQuery(id+"F0.wireOp",EDGE,"E0")])]})}),makeQuery(id+"F6.opExtrude","SWEPT_FACE",FACE,{"disambiguationData":[OSD([sQuery(id+"F5.wireOp",EDGE,"E15.sketch_text.stroke-13")])]})]});}
            var Q34;
            {var subQ0=sQuery(id+"F2.wireOp",EDGE,"E4.bottom");var subQ2=sQuery(id+"F2.wireOp",EDGE,"E5.right");var subQ3=makeQuery(id+"F2.imprint","INTERSECT",VERTEX,{"derivedFrom":[subQ0,subQ2]});Q34=makeQuery(id+"F6.boolean.opBoolean","INTERSECT",EDGE,{"derivedFrom":[makeQuery(id+"F3.boolean.opBoolean","SPLIT",FACE,{"disambiguationData":[TD([makeQuery(id+"F3.opExtrude","SWEPT_FACE",FACE,{"disambiguationData":[OSD([subQ2]),TDD([makeQuery(id+"F2.imprint","IMPRINT",EDGE,{"disambiguationData":[TD([[subQ3,1.0]])],"derivedFrom":subQ2})])]})])],"derivedFrom":makeQuery(id+"F1.opRevolve","SWEPT_FACE",FACE,{"disambiguationData":[OSD([sQuery(id+"F0.wireOp",EDGE,"E0")])]})}),makeQuery(id+"F6.opExtrude","SWEPT_FACE",FACE,{"disambiguationData":[OSD([sQuery(id+"F5.wireOp",EDGE,"E15.sketch_text.stroke-22")])]})]});}
            var Q35;
            {var subQ0=sQuery(id+"F2.wireOp",EDGE,"E4.bottom");var subQ2=sQuery(id+"F2.wireOp",EDGE,"E5.right");var subQ3=makeQuery(id+"F2.imprint","INTERSECT",VERTEX,{"derivedFrom":[subQ0,subQ2]});Q35=makeQuery(id+"F6.boolean.opBoolean","INTERSECT",EDGE,{"derivedFrom":[makeQuery(id+"F3.boolean.opBoolean","SPLIT",FACE,{"disambiguationData":[TD([makeQuery(id+"F3.opExtrude","SWEPT_FACE",FACE,{"disambiguationData":[OSD([subQ2]),TDD([makeQuery(id+"F2.imprint","IMPRINT",EDGE,{"disambiguationData":[TD([[subQ3,1.0]])],"derivedFrom":subQ2})])]})])],"derivedFrom":makeQuery(id+"F1.opRevolve","SWEPT_FACE",FACE,{"disambiguationData":[OSD([sQuery(id+"F0.wireOp",EDGE,"E0")])]})}),makeQuery(id+"F6.opExtrude","SWEPT_FACE",FACE,{"disambiguationData":[OSD([sQuery(id+"F5.wireOp",EDGE,"E15.sketch_text.stroke-23")])]})]});}
            var Q36;
            {var subQ0=sQuery(id+"F2.wireOp",EDGE,"E4.bottom");var subQ2=sQuery(id+"F2.wireOp",EDGE,"E5.right");var subQ3=makeQuery(id+"F2.imprint","INTERSECT",VERTEX,{"derivedFrom":[subQ0,subQ2]});Q36=makeQuery(id+"F6.boolean.opBoolean","INTERSECT",EDGE,{"derivedFrom":[makeQuery(id+"F3.boolean.opBoolean","SPLIT",FACE,{"disambiguationData":[TD([makeQuery(id+"F3.opExtrude","SWEPT_FACE",FACE,{"disambiguationData":[OSD([subQ2]),TDD([makeQuery(id+"F2.imprint","IMPRINT",EDGE,{"disambiguationData":[TD([[subQ3,1.0]])],"derivedFrom":subQ2})])]})])],"derivedFrom":makeQuery(id+"F1.opRevolve","SWEPT_FACE",FACE,{"disambiguationData":[OSD([sQuery(id+"F0.wireOp",EDGE,"E0")])]})}),makeQuery(id+"F6.opExtrude","SWEPT_FACE",FACE,{"disambiguationData":[OSD([sQuery(id+"F5.wireOp",EDGE,"E15.sketch_text.stroke-24")])]})]});}
            var Q37;
            {var subQ0=sQuery(id+"F2.wireOp",EDGE,"E4.bottom");var subQ2=sQuery(id+"F2.wireOp",EDGE,"E5.right");var subQ3=makeQuery(id+"F2.imprint","INTERSECT",VERTEX,{"derivedFrom":[subQ0,subQ2]});Q37=makeQuery(id+"F6.boolean.opBoolean","INTERSECT",EDGE,{"derivedFrom":[makeQuery(id+"F3.boolean.opBoolean","SPLIT",FACE,{"disambiguationData":[TD([makeQuery(id+"F3.opExtrude","SWEPT_FACE",FACE,{"disambiguationData":[OSD([subQ2]),TDD([makeQuery(id+"F2.imprint","IMPRINT",EDGE,{"disambiguationData":[TD([[subQ3,1.0]])],"derivedFrom":subQ2})])]})])],"derivedFrom":makeQuery(id+"F1.opRevolve","SWEPT_FACE",FACE,{"disambiguationData":[OSD([sQuery(id+"F0.wireOp",EDGE,"E0")])]})}),makeQuery(id+"F6.opExtrude","SWEPT_FACE",FACE,{"disambiguationData":[OSD([sQuery(id+"F5.wireOp",EDGE,"E15.sketch_text.stroke-20")])]})]});}
            var Q38;
            {var subQ0=sQuery(id+"F2.wireOp",EDGE,"E4.bottom");var subQ2=sQuery(id+"F2.wireOp",EDGE,"E5.right");var subQ3=makeQuery(id+"F2.imprint","INTERSECT",VERTEX,{"derivedFrom":[subQ0,subQ2]});Q38=makeQuery(id+"F6.boolean.opBoolean","INTERSECT",EDGE,{"derivedFrom":[makeQuery(id+"F3.boolean.opBoolean","SPLIT",FACE,{"disambiguationData":[TD([makeQuery(id+"F3.opExtrude","SWEPT_FACE",FACE,{"disambiguationData":[OSD([subQ2]),TDD([makeQuery(id+"F2.imprint","IMPRINT",EDGE,{"disambiguationData":[TD([[subQ3,1.0]])],"derivedFrom":subQ2})])]})])],"derivedFrom":makeQuery(id+"F1.opRevolve","SWEPT_FACE",FACE,{"disambiguationData":[OSD([sQuery(id+"F0.wireOp",EDGE,"E0")])]})}),makeQuery(id+"F6.opExtrude","SWEPT_FACE",FACE,{"disambiguationData":[OSD([sQuery(id+"F5.wireOp",EDGE,"E15.sketch_text.stroke-21")])]})]});}
            var Q39;
            {var subQ0=sQuery(id+"F2.wireOp",EDGE,"E4.bottom");var subQ2=sQuery(id+"F2.wireOp",EDGE,"E5.right");var subQ3=makeQuery(id+"F2.imprint","INTERSECT",VERTEX,{"derivedFrom":[subQ0,subQ2]});Q39=makeQuery(id+"F6.boolean.opBoolean","INTERSECT",EDGE,{"derivedFrom":[makeQuery(id+"F3.boolean.opBoolean","SPLIT",FACE,{"disambiguationData":[TD([makeQuery(id+"F3.opExtrude","SWEPT_FACE",FACE,{"disambiguationData":[OSD([subQ2]),TDD([makeQuery(id+"F2.imprint","IMPRINT",EDGE,{"disambiguationData":[TD([[subQ3,1.0]])],"derivedFrom":subQ2})])]})])],"derivedFrom":makeQuery(id+"F1.opRevolve","SWEPT_FACE",FACE,{"disambiguationData":[OSD([sQuery(id+"F0.wireOp",EDGE,"E0")])]})}),makeQuery(id+"F6.opExtrude","SWEPT_FACE",FACE,{"disambiguationData":[OSD([sQuery(id+"F5.wireOp",EDGE,"E15.sketch_text.stroke-7")])]})]});}
            var Q40;
            {var subQ0=sQuery(id+"F2.wireOp",EDGE,"E4.bottom");var subQ2=sQuery(id+"F2.wireOp",EDGE,"E5.right");var subQ3=makeQuery(id+"F2.imprint","INTERSECT",VERTEX,{"derivedFrom":[subQ0,subQ2]});Q40=makeQuery(id+"F6.boolean.opBoolean","INTERSECT",EDGE,{"derivedFrom":[makeQuery(id+"F3.boolean.opBoolean","SPLIT",FACE,{"disambiguationData":[TD([makeQuery(id+"F3.opExtrude","SWEPT_FACE",FACE,{"disambiguationData":[OSD([subQ2]),TDD([makeQuery(id+"F2.imprint","IMPRINT",EDGE,{"disambiguationData":[TD([[subQ3,1.0]])],"derivedFrom":subQ2})])]})])],"derivedFrom":makeQuery(id+"F1.opRevolve","SWEPT_FACE",FACE,{"disambiguationData":[OSD([sQuery(id+"F0.wireOp",EDGE,"E0")])]})}),makeQuery(id+"F6.opExtrude","SWEPT_FACE",FACE,{"disambiguationData":[OSD([sQuery(id+"F5.wireOp",EDGE,"E15.sketch_text.stroke-6")])]})]});}
            var Q41;
            {var subQ0=sQuery(id+"F2.wireOp",EDGE,"E4.bottom");var subQ2=sQuery(id+"F2.wireOp",EDGE,"E5.right");var subQ3=makeQuery(id+"F2.imprint","INTERSECT",VERTEX,{"derivedFrom":[subQ0,subQ2]});Q41=makeQuery(id+"F6.boolean.opBoolean","INTERSECT",EDGE,{"derivedFrom":[makeQuery(id+"F3.boolean.opBoolean","SPLIT",FACE,{"disambiguationData":[TD([makeQuery(id+"F3.opExtrude","SWEPT_FACE",FACE,{"disambiguationData":[OSD([subQ2]),TDD([makeQuery(id+"F2.imprint","IMPRINT",EDGE,{"disambiguationData":[TD([[subQ3,1.0]])],"derivedFrom":subQ2})])]})])],"derivedFrom":makeQuery(id+"F1.opRevolve","SWEPT_FACE",FACE,{"disambiguationData":[OSD([sQuery(id+"F0.wireOp",EDGE,"E0")])]})}),makeQuery(id+"F6.opExtrude","SWEPT_FACE",FACE,{"disambiguationData":[OSD([sQuery(id+"F5.wireOp",EDGE,"E15.sketch_text.stroke-5")])]})]});}
            var Q42;
            {var subQ0=sQuery(id+"F2.wireOp",EDGE,"E4.bottom");var subQ2=sQuery(id+"F2.wireOp",EDGE,"E5.right");var subQ3=makeQuery(id+"F2.imprint","INTERSECT",VERTEX,{"derivedFrom":[subQ0,subQ2]});Q42=makeQuery(id+"F6.boolean.opBoolean","INTERSECT",EDGE,{"derivedFrom":[makeQuery(id+"F3.boolean.opBoolean","SPLIT",FACE,{"disambiguationData":[TD([makeQuery(id+"F3.opExtrude","SWEPT_FACE",FACE,{"disambiguationData":[OSD([subQ2]),TDD([makeQuery(id+"F2.imprint","IMPRINT",EDGE,{"disambiguationData":[TD([[subQ3,1.0]])],"derivedFrom":subQ2})])]})])],"derivedFrom":makeQuery(id+"F1.opRevolve","SWEPT_FACE",FACE,{"disambiguationData":[OSD([sQuery(id+"F0.wireOp",EDGE,"E0")])]})}),makeQuery(id+"F6.opExtrude","SWEPT_FACE",FACE,{"disambiguationData":[OSD([sQuery(id+"F5.wireOp",EDGE,"E15.sketch_text.stroke-8")])]})]});}
            var Q43;
            {var subQ0=sQuery(id+"F2.wireOp",EDGE,"E4.bottom");var subQ2=sQuery(id+"F2.wireOp",EDGE,"E5.right");var subQ3=makeQuery(id+"F2.imprint","INTERSECT",VERTEX,{"derivedFrom":[subQ0,subQ2]});Q43=makeQuery(id+"F6.boolean.opBoolean","INTERSECT",EDGE,{"derivedFrom":[makeQuery(id+"F3.boolean.opBoolean","SPLIT",FACE,{"disambiguationData":[TD([makeQuery(id+"F3.opExtrude","SWEPT_FACE",FACE,{"disambiguationData":[OSD([subQ2]),TDD([makeQuery(id+"F2.imprint","IMPRINT",EDGE,{"disambiguationData":[TD([[subQ3,1.0]])],"derivedFrom":subQ2})])]})])],"derivedFrom":makeQuery(id+"F1.opRevolve","SWEPT_FACE",FACE,{"disambiguationData":[OSD([sQuery(id+"F0.wireOp",EDGE,"E0")])]})}),makeQuery(id+"F6.opExtrude","SWEPT_FACE",FACE,{"disambiguationData":[OSD([sQuery(id+"F5.wireOp",EDGE,"E15.sketch_text.stroke-10")])]})]});}
            var Q44;
            {var subQ0=sQuery(id+"F2.wireOp",EDGE,"E4.bottom");var subQ2=sQuery(id+"F2.wireOp",EDGE,"E5.right");var subQ3=makeQuery(id+"F2.imprint","INTERSECT",VERTEX,{"derivedFrom":[subQ0,subQ2]});Q44=makeQuery(id+"F6.boolean.opBoolean","INTERSECT",EDGE,{"derivedFrom":[makeQuery(id+"F3.boolean.opBoolean","SPLIT",FACE,{"disambiguationData":[TD([makeQuery(id+"F3.opExtrude","SWEPT_FACE",FACE,{"disambiguationData":[OSD([subQ2]),TDD([makeQuery(id+"F2.imprint","IMPRINT",EDGE,{"disambiguationData":[TD([[subQ3,1.0]])],"derivedFrom":subQ2})])]})])],"derivedFrom":makeQuery(id+"F1.opRevolve","SWEPT_FACE",FACE,{"disambiguationData":[OSD([sQuery(id+"F0.wireOp",EDGE,"E0")])]})}),makeQuery(id+"F6.opExtrude","SWEPT_FACE",FACE,{"disambiguationData":[OSD([sQuery(id+"F5.wireOp",EDGE,"E15.sketch_text.stroke-9")])]})]});}
            var Q45;
            {var subQ0=sQuery(id+"F2.wireOp",EDGE,"E4.bottom");var subQ2=sQuery(id+"F2.wireOp",EDGE,"E5.right");var subQ3=makeQuery(id+"F2.imprint","INTERSECT",VERTEX,{"derivedFrom":[subQ0,subQ2]});Q45=makeQuery(id+"F6.boolean.opBoolean","INTERSECT",EDGE,{"derivedFrom":[makeQuery(id+"F3.boolean.opBoolean","SPLIT",FACE,{"disambiguationData":[TD([makeQuery(id+"F3.opExtrude","SWEPT_FACE",FACE,{"disambiguationData":[OSD([subQ2]),TDD([makeQuery(id+"F2.imprint","IMPRINT",EDGE,{"disambiguationData":[TD([[subQ3,1.0]])],"derivedFrom":subQ2})])]})])],"derivedFrom":makeQuery(id+"F1.opRevolve","SWEPT_FACE",FACE,{"disambiguationData":[OSD([sQuery(id+"F0.wireOp",EDGE,"E0")])]})}),makeQuery(id+"F6.opExtrude","SWEPT_FACE",FACE,{"disambiguationData":[OSD([sQuery(id+"F5.wireOp",EDGE,"E15.sketch_text.stroke-11")])]})]});}
            var Q46;
            {var subQ0=sQuery(id+"F2.wireOp",EDGE,"E4.bottom");var subQ2=sQuery(id+"F2.wireOp",EDGE,"E5.right");var subQ3=makeQuery(id+"F2.imprint","INTERSECT",VERTEX,{"derivedFrom":[subQ0,subQ2]});Q46=makeQuery(id+"F6.boolean.opBoolean","INTERSECT",EDGE,{"derivedFrom":[makeQuery(id+"F3.boolean.opBoolean","SPLIT",FACE,{"disambiguationData":[TD([makeQuery(id+"F3.opExtrude","SWEPT_FACE",FACE,{"disambiguationData":[OSD([subQ2]),TDD([makeQuery(id+"F2.imprint","IMPRINT",EDGE,{"disambiguationData":[TD([[subQ3,1.0]])],"derivedFrom":subQ2})])]})])],"derivedFrom":makeQuery(id+"F1.opRevolve","SWEPT_FACE",FACE,{"disambiguationData":[OSD([sQuery(id+"F0.wireOp",EDGE,"E0")])]})}),makeQuery(id+"F6.opExtrude","SWEPT_FACE",FACE,{"disambiguationData":[OSD([sQuery(id+"F5.wireOp",EDGE,"E15.sketch_text.stroke-0")])]})]});}
            var Q47;
            {var subQ0=sQuery(id+"F2.wireOp",EDGE,"E4.bottom");var subQ2=sQuery(id+"F2.wireOp",EDGE,"E5.right");var subQ3=makeQuery(id+"F2.imprint","INTERSECT",VERTEX,{"derivedFrom":[subQ0,subQ2]});Q47=makeQuery(id+"F6.boolean.opBoolean","INTERSECT",EDGE,{"derivedFrom":[makeQuery(id+"F3.boolean.opBoolean","SPLIT",FACE,{"disambiguationData":[TD([makeQuery(id+"F3.opExtrude","SWEPT_FACE",FACE,{"disambiguationData":[OSD([subQ2]),TDD([makeQuery(id+"F2.imprint","IMPRINT",EDGE,{"disambiguationData":[TD([[subQ3,1.0]])],"derivedFrom":subQ2})])]})])],"derivedFrom":makeQuery(id+"F1.opRevolve","SWEPT_FACE",FACE,{"disambiguationData":[OSD([sQuery(id+"F0.wireOp",EDGE,"E0")])]})}),makeQuery(id+"F6.opExtrude","SWEPT_FACE",FACE,{"disambiguationData":[OSD([sQuery(id+"F5.wireOp",EDGE,"E15.sketch_text.stroke-1")])]})]});}
            var Q48;
            {var subQ0=sQuery(id+"F2.wireOp",EDGE,"E4.bottom");var subQ2=sQuery(id+"F2.wireOp",EDGE,"E5.right");var subQ3=makeQuery(id+"F2.imprint","INTERSECT",VERTEX,{"derivedFrom":[subQ0,subQ2]});Q48=makeQuery(id+"F6.boolean.opBoolean","INTERSECT",EDGE,{"derivedFrom":[makeQuery(id+"F3.boolean.opBoolean","SPLIT",FACE,{"disambiguationData":[TD([makeQuery(id+"F3.opExtrude","SWEPT_FACE",FACE,{"disambiguationData":[OSD([subQ2]),TDD([makeQuery(id+"F2.imprint","IMPRINT",EDGE,{"disambiguationData":[TD([[subQ3,1.0]])],"derivedFrom":subQ2})])]})])],"derivedFrom":makeQuery(id+"F1.opRevolve","SWEPT_FACE",FACE,{"disambiguationData":[OSD([sQuery(id+"F0.wireOp",EDGE,"E0")])]})}),makeQuery(id+"F6.opExtrude","SWEPT_FACE",FACE,{"disambiguationData":[OSD([sQuery(id+"F5.wireOp",EDGE,"E15.sketch_text.stroke-2")])]})]});}
            var Q49;
            {var subQ0=sQuery(id+"F2.wireOp",EDGE,"E4.bottom");var subQ2=sQuery(id+"F2.wireOp",EDGE,"E5.right");var subQ3=makeQuery(id+"F2.imprint","INTERSECT",VERTEX,{"derivedFrom":[subQ0,subQ2]});Q49=makeQuery(id+"F6.boolean.opBoolean","INTERSECT",EDGE,{"derivedFrom":[makeQuery(id+"F3.boolean.opBoolean","SPLIT",FACE,{"disambiguationData":[TD([makeQuery(id+"F3.opExtrude","SWEPT_FACE",FACE,{"disambiguationData":[OSD([subQ2]),TDD([makeQuery(id+"F2.imprint","IMPRINT",EDGE,{"disambiguationData":[TD([[subQ3,1.0]])],"derivedFrom":subQ2})])]})])],"derivedFrom":makeQuery(id+"F1.opRevolve","SWEPT_FACE",FACE,{"disambiguationData":[OSD([sQuery(id+"F0.wireOp",EDGE,"E0")])]})}),makeQuery(id+"F6.opExtrude","SWEPT_FACE",FACE,{"disambiguationData":[OSD([sQuery(id+"F5.wireOp",EDGE,"E15.sketch_text.stroke-3")])]})]});}
            var Q50;
            {var subQ0=sQuery(id+"F2.wireOp",EDGE,"E4.bottom");var subQ2=sQuery(id+"F2.wireOp",EDGE,"E5.right");var subQ3=makeQuery(id+"F2.imprint","INTERSECT",VERTEX,{"derivedFrom":[subQ0,subQ2]});Q50=makeQuery(id+"F6.boolean.opBoolean","INTERSECT",EDGE,{"derivedFrom":[makeQuery(id+"F3.boolean.opBoolean","SPLIT",FACE,{"disambiguationData":[TD([makeQuery(id+"F3.opExtrude","SWEPT_FACE",FACE,{"disambiguationData":[OSD([subQ2]),TDD([makeQuery(id+"F2.imprint","IMPRINT",EDGE,{"disambiguationData":[TD([[subQ3,1.0]])],"derivedFrom":subQ2})])]})])],"derivedFrom":makeQuery(id+"F1.opRevolve","SWEPT_FACE",FACE,{"disambiguationData":[OSD([sQuery(id+"F0.wireOp",EDGE,"E0")])]})}),makeQuery(id+"F6.opExtrude","SWEPT_FACE",FACE,{"disambiguationData":[OSD([sQuery(id+"F5.wireOp",EDGE,"E15.sketch_text.stroke-4")])]})]});}
            fillet(context, id + "F8", {"entities" : qUnion([Q0, Q1, Q2, Q3, Q4, Q5, Q6, Q7, Q8, Q9, Q10, Q11, Q12, Q13, Q14, Q15, Q16, Q17, Q18, Q19, Q20, Q21, Q22, Q23, Q24, Q25, Q26, Q27, Q28, Q29, Q30, Q31, Q32, Q33, Q34, Q35, Q36, Q37, Q38, Q39, Q40, Q41, Q42, Q43, Q44, Q45, Q46, Q47, Q48, Q49, Q50]), "radius" : 5.08 * mm, "tangentPropagation" : true, "allowEdgeOverflow" : false});
        }
    });
